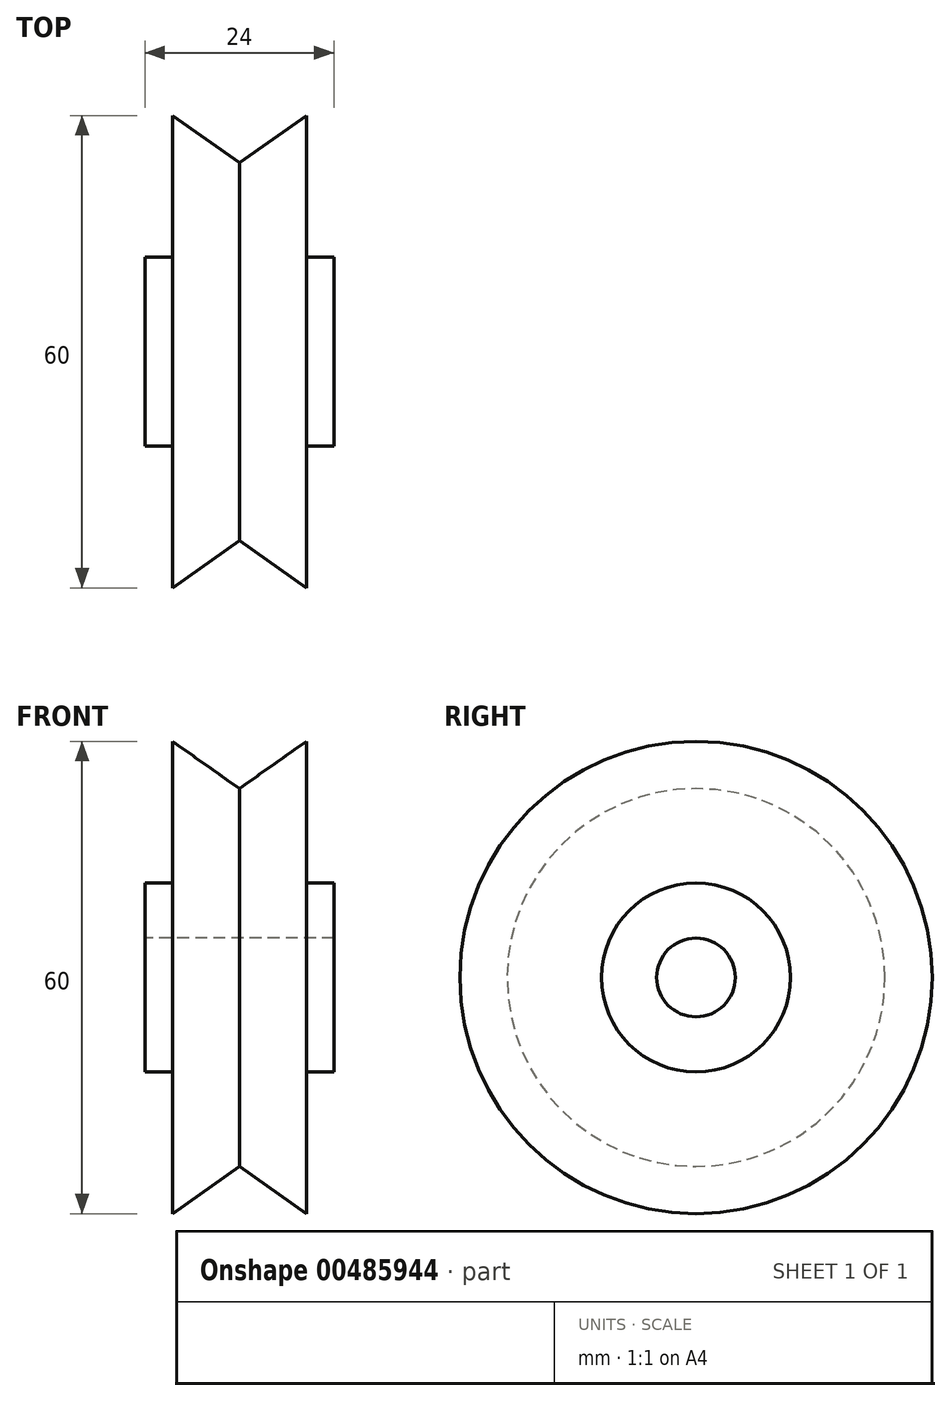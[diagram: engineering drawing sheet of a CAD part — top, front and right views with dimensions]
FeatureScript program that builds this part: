
annotation { "Feature Type Name" : "Feature", "Feature Type Description" : "" }
export const myFeature = defineFeature(function(context is Context, id is Id, definition is map)
    precondition{}
    {
        {
            var Q0;
            Q0=qCreatedBy(makeId("Top.planeOp"),FACE);
            var sketch = newSketch(context, id + "F0", { "sketchPlane" : qUnion([Q0])});
            skLineSegment(sketch, "E0", {"start": v(0, 47.97) * mm, "end": v(0, -45.27) * mm, "construction": true});
            skLineSegment(sketch, "E1", {"start": v(-40.81, 0) * mm, "end": v(48.24, 0) * mm, "construction": true});
            skLineSegment(sketch, "E2", {"start": v(-12, 5) * mm, "end": v(0, 5) * mm});
            skLineSegment(sketch, "E3", {"start": v(-12, 5) * mm, "end": v(-12, 12) * mm});
            skLineSegment(sketch, "E4", {"start": v(-12, 12) * mm, "end": v(-8.5, 12) * mm});
            skLineSegment(sketch, "E5", {"start": v(-8.5, 12) * mm, "end": v(-8.5, 30) * mm});
            skLineSegment(sketch, "E6", {"start": v(-8.5, 30) * mm, "end": v(0, 24) * mm});
            skLineSegment(sketch, "E7.MirrorCS", {"start": v(8.5, 30) * mm, "end": v(0, 24) * mm});
            skLineSegment(sketch, "E8.MirrorCS", {"start": v(8.5, 12) * mm, "end": v(8.5, 30) * mm});
            skLineSegment(sketch, "E9.MirrorCS", {"start": v(12, 5) * mm, "end": v(0, 5) * mm});
            skLineSegment(sketch, "E10.MirrorCS", {"start": v(12, 5) * mm, "end": v(12, 12) * mm});
            skLineSegment(sketch, "E11.MirrorCS", {"start": v(12, 12) * mm, "end": v(8.5, 12) * mm});
            skSolve(sketch);
        }
        {
            var Q0;
            Q0=makeQuery(id+"F0.imprint","IMPRINT",FACE,{"disambiguationData":[TD([[makeQuery(id+"F0.imprint","IMPRINT",EDGE,{"derivedFrom":sQuery(id+"F0.wireOp",EDGE,"E2")}),1.0]])]});
            var Q1;
            Q1=sQuery(id+"F0.wireOp",EDGE,"E1");
            revolve(context, id + "F1", {"entities" : qUnion([Q0]), "axis" : qUnion([Q1]), "revolveType" : RevolveType.FULL});
        }
    });
